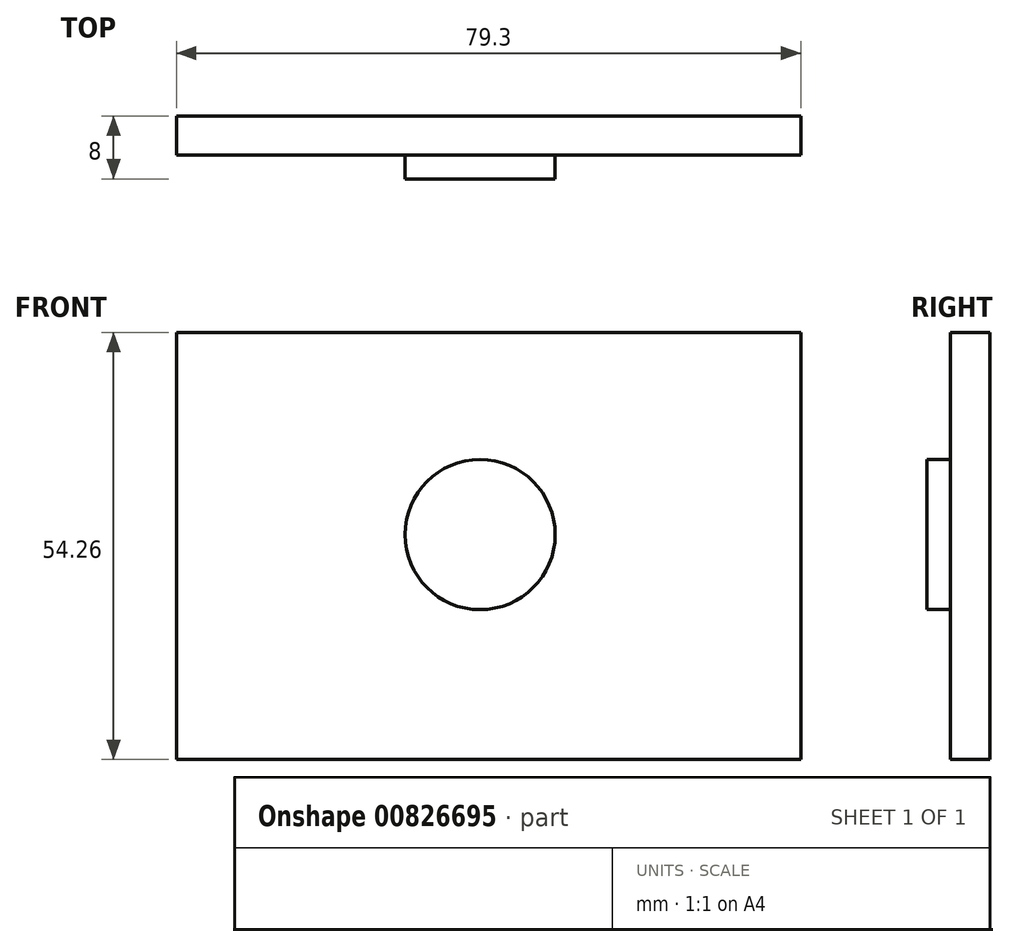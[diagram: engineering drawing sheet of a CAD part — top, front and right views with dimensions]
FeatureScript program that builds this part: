
annotation { "Feature Type Name" : "Feature", "Feature Type Description" : "" }
export const myFeature = defineFeature(function(context is Context, id is Id, definition is map)
    precondition{}
    {
        {
            var Q0;
            Q0=qCreatedBy(makeId("Front.planeOp"),FACE);
            var sketch = newSketch(context, id + "F0", { "sketchPlane" : qUnion([Q0])});
            skLineSegment(sketch, "E0.bottom", {"start": v(-38.56, 25.68) * mm, "end": v(40.74, 25.68) * mm});
            skLineSegment(sketch, "E0.top", {"start": v(-38.56, -28.58) * mm, "end": v(40.74, -28.58) * mm});
            skLineSegment(sketch, "E0.left", {"start": v(-38.56, 25.68) * mm, "end": v(-38.56, -28.58) * mm});
            skLineSegment(sketch, "E0.right", {"start": v(40.74, 25.68) * mm, "end": v(40.74, -28.58) * mm});
            skSolve(sketch);
        }
        {
            var Q0;
            Q0=makeQuery(id+"F0.imprint","IMPRINT",FACE,{"disambiguationData":[TD([[makeQuery(id+"F0.imprint","IMPRINT",EDGE,{"derivedFrom":sQuery(id+"F0.wireOp",EDGE,"E0.bottom")}),-1.0]])]});
            extrude(context, id + "F1", {"entities" : qUnion([Q0]), "oppositeDirection" : true, "depth" : 5 * mm, "offsetDistance" : 25 * mm});
        }
        {
            var Q0;
            Q0=makeQuery(id+"F1.opExtrude","CAP_FACE",FACE,{"disambiguationData":[OSD([sQuery(id+"F0.wireOp",EDGE,"E0.bottom"),sQuery(id+"F0.wireOp",EDGE,"E0.top"),sQuery(id+"F0.wireOp",EDGE,"E0.left"),sQuery(id+"F0.wireOp",EDGE,"E0.right")])],"isStart":true});
            var sketch = newSketch(context, id + "F2", { "sketchPlane" : qUnion([Q0])});
            skCircle(sketch, "E1", {"center": v(0, 0) * mm, "radius": 9.54 * mm});
            skSolve(sketch);
        }
        {
            var Q0;
            Q0 = qSketchRegion(id + "F2", true);
            extrude(context, id + "F3", {"entities" : qUnion([Q0]), "operationType" : NewBodyOperationType.ADD, "depth" : 3 * mm, "offsetDistance" : 25 * mm});
        }
        {
            var Q0;
            Q0=makeQuery(id+"F1.opExtrude","CAP_FACE",FACE,{"disambiguationData":[OSD([sQuery(id+"F0.wireOp",EDGE,"E0.bottom"),sQuery(id+"F0.wireOp",EDGE,"E0.top"),sQuery(id+"F0.wireOp",EDGE,"E0.left"),sQuery(id+"F0.wireOp",EDGE,"E0.right")])],"isStart":true});
            var sketch = newSketch(context, id + "F4", { "sketchPlane" : qUnion([Q0])});
            skCircle(sketch, "E2", {"center": v(0, 0) * mm, "radius": 14.6 * mm});
            skSolve(sketch);
        }
        {
            var Q0;
            Q0=sQuery(id+"F4.wireOp",EDGE,"E2");
            extrude(context, id + "F5", {"bodyType" : ToolBodyType.SURFACE, "surfaceEntities" : qUnion([Q0]), "depth" : 5 * mm, "offsetDistance" : 25 * mm});
        }
    });
